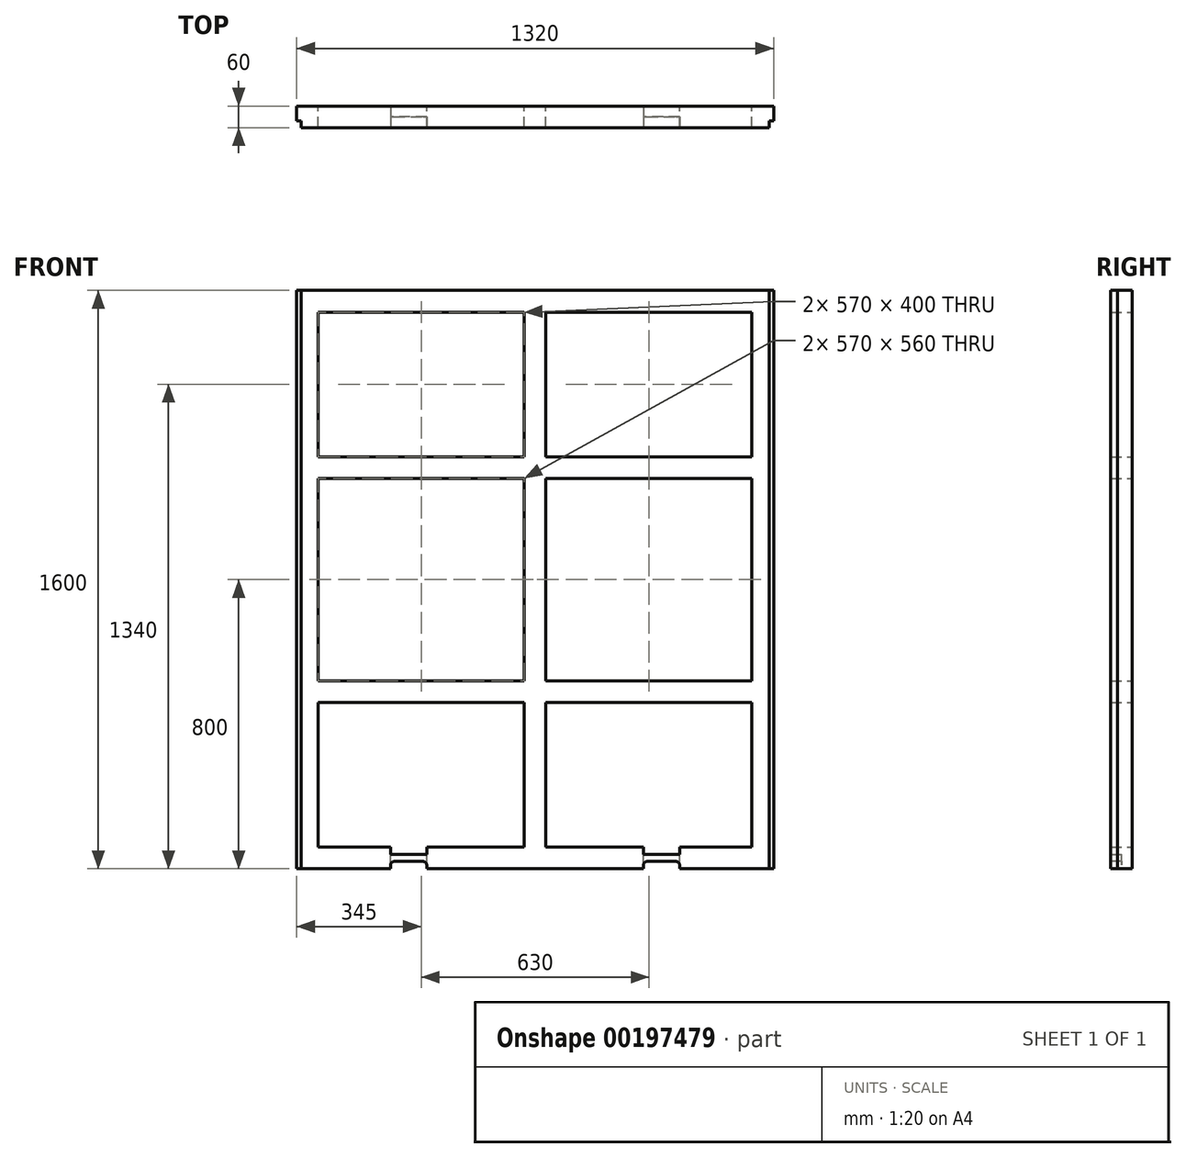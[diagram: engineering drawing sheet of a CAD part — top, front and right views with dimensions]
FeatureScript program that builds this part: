
annotation { "Feature Type Name" : "Feature", "Feature Type Description" : "" }
export const myFeature = defineFeature(function(context is Context, id is Id, definition is map)
    precondition{}
    {
        {
            var Q0;
            Q0=qCreatedBy(makeId("Front.planeOp"),FACE);
            var sketch = newSketch(context, id + "F0", { "sketchPlane" : qUnion([Q0])});
            skLineSegment(sketch, "E0.bottom", {"start": v(660, -800) * mm, "end": v(-660, -800) * mm});
            skLineSegment(sketch, "E0.top", {"start": v(660, 800) * mm, "end": v(-660, 800) * mm});
            skLineSegment(sketch, "E0.left", {"start": v(660, -800) * mm, "end": v(660, 800) * mm});
            skLineSegment(sketch, "E0.right", {"start": v(-660, -800) * mm, "end": v(-660, 800) * mm});
            skPoint(sketch, "E0.middle", {"position": v(0, 0) * mm});
            skLineSegment(sketch, "E1.0", {"start": v(600, 740) * mm, "end": v(30, 740) * mm});
            skLineSegment(sketch, "E1.1", {"start": v(600, -740) * mm, "end": v(600, -340) * mm});
            skLineSegment(sketch, "E1.2", {"start": v(600, -740) * mm, "end": v(30, -740) * mm});
            skLineSegment(sketch, "E1.3", {"start": v(-600, -740) * mm, "end": v(-600, -340) * mm});
            skLineSegment(sketch, "E2", {"start": v(-600, 340) * mm, "end": v(-30, 340) * mm});
            skLineSegment(sketch, "E3", {"start": v(-600, -340) * mm, "end": v(-30, -340) * mm});
            skLineSegment(sketch, "E4.0", {"start": v(-30, 740) * mm, "end": v(-30, 340) * mm});
            skLineSegment(sketch, "E5.0", {"start": v(30, 740) * mm, "end": v(30, 340) * mm});
            skLineSegment(sketch, "E6.0", {"start": v(-600, -280) * mm, "end": v(-30, -280) * mm});
            skPoint(sketch, "E7.orphan", {"position": v(0, 740) * mm});
            skLineSegment(sketch, "E8.trimOffspring", {"start": v(30, 340) * mm, "end": v(600, 340) * mm});
            skLineSegment(sketch, "E9.trimOffspring", {"start": v(-30, 280) * mm, "end": v(-30, -280) * mm});
            skLineSegment(sketch, "E10.trimOffspring", {"start": v(30, 280) * mm, "end": v(600, 280) * mm});
            skLineSegment(sketch, "E11.trimOffspring", {"start": v(30, 280) * mm, "end": v(30, -280) * mm});
            skLineSegment(sketch, "E12.trimOffspring", {"start": v(30, -280) * mm, "end": v(600, -280) * mm});
            skLineSegment(sketch, "E13.trimOffspring", {"start": v(30, -340) * mm, "end": v(30, -740) * mm});
            skLineSegment(sketch, "E14.trimOffspring", {"start": v(-30, -340) * mm, "end": v(-30, -740) * mm});
            skLineSegment(sketch, "E15.trimOffspring", {"start": v(30, -340) * mm, "end": v(600, -340) * mm});
            skPoint(sketch, "E16.orphan", {"position": v(0, -740) * mm});
            skLineSegment(sketch, "E17", {"start": v(-30, 280) * mm, "end": v(-600, 280) * mm});
            skLineSegment(sketch, "E18.trimOffspring", {"start": v(-30, 740) * mm, "end": v(-600, 740) * mm});
            skLineSegment(sketch, "E19.trimOffspring", {"start": v(600, 340) * mm, "end": v(600, 740) * mm});
            skLineSegment(sketch, "E20.trimOffspring", {"start": v(600, -280) * mm, "end": v(600, 280) * mm});
            skLineSegment(sketch, "E21.trimOffspring", {"start": v(-600, -280) * mm, "end": v(-600, 280) * mm});
            skLineSegment(sketch, "E22.trimOffspring", {"start": v(-600, 340) * mm, "end": v(-600, 740) * mm});
            skLineSegment(sketch, "E23.trimOffspring", {"start": v(-30, -740) * mm, "end": v(-600, -740) * mm});
            skSolve(sketch);
        }
        {
            var Q0;
            Q0 = qSketchRegion(id + "F0", true);
            extrude(context, id + "F1", {"entities" : qUnion([Q0]), "depth" : 60 * mm});
        }
        {
            var Q0;
            Q0=makeQuery(id+"F1.opExtrude","CAP_FACE",FACE,{"disambiguationData":[OSD([sQuery(id+"F0.wireOp",EDGE,"E0.bottom"),sQuery(id+"F0.wireOp",EDGE,"E0.top"),sQuery(id+"F0.wireOp",EDGE,"E0.left"),sQuery(id+"F0.wireOp",EDGE,"E0.right"),sQuery(id+"F0.wireOp",EDGE,"E1.0"),sQuery(id+"F0.wireOp",EDGE,"E1.1"),sQuery(id+"F0.wireOp",EDGE,"E1.2"),sQuery(id+"F0.wireOp",EDGE,"E1.3"),sQuery(id+"F0.wireOp",EDGE,"E2"),sQuery(id+"F0.wireOp",EDGE,"E3"),sQuery(id+"F0.wireOp",EDGE,"E4.0"),sQuery(id+"F0.wireOp",EDGE,"E5.0"),sQuery(id+"F0.wireOp",EDGE,"E6.0"),sQuery(id+"F0.wireOp",EDGE,"E8.trimOffspring"),sQuery(id+"F0.wireOp",EDGE,"E9.trimOffspring"),sQuery(id+"F0.wireOp",EDGE,"E10.trimOffspring"),sQuery(id+"F0.wireOp",EDGE,"E11.trimOffspring"),sQuery(id+"F0.wireOp",EDGE,"E12.trimOffspring"),sQuery(id+"F0.wireOp",EDGE,"E13.trimOffspring"),sQuery(id+"F0.wireOp",EDGE,"E14.trimOffspring"),sQuery(id+"F0.wireOp",EDGE,"E15.trimOffspring"),sQuery(id+"F0.wireOp",EDGE,"E17"),sQuery(id+"F0.wireOp",EDGE,"E18.trimOffspring"),sQuery(id+"F0.wireOp",EDGE,"E19.trimOffspring"),sQuery(id+"F0.wireOp",EDGE,"E20.trimOffspring"),sQuery(id+"F0.wireOp",EDGE,"E21.trimOffspring"),sQuery(id+"F0.wireOp",EDGE,"E22.trimOffspring"),sQuery(id+"F0.wireOp",EDGE,"E23.trimOffspring")])],"isStart":false});
            var sketch = newSketch(context, id + "F2", { "sketchPlane" : qUnion([Q0])});
            skLineSegment(sketch, "E24.bottom", {"start": v(-660, -800) * mm, "end": v(-648, -800) * mm});
            skLineSegment(sketch, "E24.top", {"start": v(-660, 800) * mm, "end": v(-648, 800) * mm});
            skLineSegment(sketch, "E24.left", {"start": v(-660, -800) * mm, "end": v(-660, 800) * mm});
            skLineSegment(sketch, "E24.right", {"start": v(-648, -800) * mm, "end": v(-648, 800) * mm});
            skLineSegment(sketch, "E25.bottom", {"start": v(660, -800) * mm, "end": v(648, -800) * mm});
            skLineSegment(sketch, "E25.top", {"start": v(660, 800) * mm, "end": v(648, 800) * mm});
            skLineSegment(sketch, "E25.left", {"start": v(660, -800) * mm, "end": v(660, 800) * mm});
            skLineSegment(sketch, "E25.right", {"start": v(648, -800) * mm, "end": v(648, 800) * mm});
            skSolve(sketch);
        }
        {
            var Q0;
            Q0 = qSketchRegion(id + "F2", true);
            extrude(context, id + "F3", {"entities" : qUnion([Q0]), "operationType" : NewBodyOperationType.REMOVE, "oppositeDirection" : true, "depth" : 19 * mm});
        }
        {
            var Q0;
            Q0=makeQuery(id+"F1.opExtrude","CAP_FACE",FACE,{"disambiguationData":[OSD([sQuery(id+"F0.wireOp",EDGE,"E0.bottom"),sQuery(id+"F0.wireOp",EDGE,"E0.top"),sQuery(id+"F0.wireOp",EDGE,"E0.left"),sQuery(id+"F0.wireOp",EDGE,"E0.right"),sQuery(id+"F0.wireOp",EDGE,"E1.0"),sQuery(id+"F0.wireOp",EDGE,"E1.1"),sQuery(id+"F0.wireOp",EDGE,"E1.2"),sQuery(id+"F0.wireOp",EDGE,"E1.3"),sQuery(id+"F0.wireOp",EDGE,"E2"),sQuery(id+"F0.wireOp",EDGE,"E3"),sQuery(id+"F0.wireOp",EDGE,"E4.0"),sQuery(id+"F0.wireOp",EDGE,"E5.0"),sQuery(id+"F0.wireOp",EDGE,"E6.0"),sQuery(id+"F0.wireOp",EDGE,"E8.trimOffspring"),sQuery(id+"F0.wireOp",EDGE,"E9.trimOffspring"),sQuery(id+"F0.wireOp",EDGE,"E10.trimOffspring"),sQuery(id+"F0.wireOp",EDGE,"E11.trimOffspring"),sQuery(id+"F0.wireOp",EDGE,"E12.trimOffspring"),sQuery(id+"F0.wireOp",EDGE,"E13.trimOffspring"),sQuery(id+"F0.wireOp",EDGE,"E14.trimOffspring"),sQuery(id+"F0.wireOp",EDGE,"E15.trimOffspring"),sQuery(id+"F0.wireOp",EDGE,"E17"),sQuery(id+"F0.wireOp",EDGE,"E18.trimOffspring"),sQuery(id+"F0.wireOp",EDGE,"E19.trimOffspring"),sQuery(id+"F0.wireOp",EDGE,"E20.trimOffspring"),sQuery(id+"F0.wireOp",EDGE,"E21.trimOffspring"),sQuery(id+"F0.wireOp",EDGE,"E22.trimOffspring"),sQuery(id+"F0.wireOp",EDGE,"E23.trimOffspring")])],"isStart":false});
            var sketch = newSketch(context, id + "F4", { "sketchPlane" : qUnion([Q0])});
            skLineSegment(sketch, "E26.bottom", {"start": v(-400, -800) * mm, "end": v(-300, -800) * mm});
            skLineSegment(sketch, "E26.top", {"start": v(-390, -780) * mm, "end": v(-310, -780) * mm});
            skLineSegment(sketch, "E26.left", {"start": v(-400, -800) * mm, "end": v(-400, -790) * mm});
            skLineSegment(sketch, "E26.right", {"start": v(-300, -800) * mm, "end": v(-300, -790) * mm});
            skLineSegment(sketch, "E27.bottom", {"start": v(300, -800) * mm, "end": v(400, -800) * mm});
            skLineSegment(sketch, "E27.top", {"start": v(310, -780) * mm, "end": v(390, -780) * mm});
            skLineSegment(sketch, "E27.left", {"start": v(300, -800) * mm, "end": v(300, -790) * mm});
            skLineSegment(sketch, "E27.right", {"start": v(400, -800) * mm, "end": v(400, -790) * mm});
            skPoint(sketch, "E28.visualSharp", {"position": v(-400, -780) * mm});
            skArc(sketch, "E28.filletArc", {"start": v(-390, -780) * mm, "mid": v(-397.07, -782.93) * mm, "end": v(-400, -790) * mm});
            skPoint(sketch, "E29.visualSharp", {"position": v(-300, -780) * mm});
            skArc(sketch, "E29.filletArc", {"start": v(-300, -790) * mm, "mid": v(-302.93, -782.93) * mm, "end": v(-310, -780) * mm});
            skPoint(sketch, "E30.visualSharp", {"position": v(300, -780) * mm});
            skArc(sketch, "E30.filletArc", {"start": v(310, -780) * mm, "mid": v(302.93, -782.93) * mm, "end": v(300, -790) * mm});
            skPoint(sketch, "E31.visualSharp", {"position": v(400, -780) * mm});
            skArc(sketch, "E31.filletArc", {"start": v(400, -790) * mm, "mid": v(397.07, -782.93) * mm, "end": v(390, -780) * mm});
            skSolve(sketch);
        }
        {
            var Q0;
            Q0 = qSketchRegion(id + "F4", true);
            extrude(context, id + "F5", {"entities" : qUnion([Q0]), "operationType" : NewBodyOperationType.REMOVE, "oppositeDirection" : true, "depth" : 60 * mm});
        }
        {
            var Q0;
            Q0=makeQuery(id+"F1.opExtrude","CAP_FACE",FACE,{"disambiguationData":[OSD([sQuery(id+"F0.wireOp",EDGE,"E0.bottom"),sQuery(id+"F0.wireOp",EDGE,"E0.top"),sQuery(id+"F0.wireOp",EDGE,"E0.left"),sQuery(id+"F0.wireOp",EDGE,"E0.right"),sQuery(id+"F0.wireOp",EDGE,"E1.0"),sQuery(id+"F0.wireOp",EDGE,"E1.1"),sQuery(id+"F0.wireOp",EDGE,"E1.2"),sQuery(id+"F0.wireOp",EDGE,"E1.3"),sQuery(id+"F0.wireOp",EDGE,"E2"),sQuery(id+"F0.wireOp",EDGE,"E3"),sQuery(id+"F0.wireOp",EDGE,"E4.0"),sQuery(id+"F0.wireOp",EDGE,"E5.0"),sQuery(id+"F0.wireOp",EDGE,"E6.0"),sQuery(id+"F0.wireOp",EDGE,"E8.trimOffspring"),sQuery(id+"F0.wireOp",EDGE,"E9.trimOffspring"),sQuery(id+"F0.wireOp",EDGE,"E10.trimOffspring"),sQuery(id+"F0.wireOp",EDGE,"E11.trimOffspring"),sQuery(id+"F0.wireOp",EDGE,"E12.trimOffspring"),sQuery(id+"F0.wireOp",EDGE,"E13.trimOffspring"),sQuery(id+"F0.wireOp",EDGE,"E14.trimOffspring"),sQuery(id+"F0.wireOp",EDGE,"E15.trimOffspring"),sQuery(id+"F0.wireOp",EDGE,"E17"),sQuery(id+"F0.wireOp",EDGE,"E18.trimOffspring"),sQuery(id+"F0.wireOp",EDGE,"E19.trimOffspring"),sQuery(id+"F0.wireOp",EDGE,"E20.trimOffspring"),sQuery(id+"F0.wireOp",EDGE,"E21.trimOffspring"),sQuery(id+"F0.wireOp",EDGE,"E22.trimOffspring"),sQuery(id+"F0.wireOp",EDGE,"E23.trimOffspring")])],"isStart":true});
            var sketch = newSketch(context, id + "F6", { "sketchPlane" : qUnion([Q0])});
            skLineSegment(sketch, "E32.bottom", {"start": v(-400, -800) * mm, "end": v(-300, -800) * mm});
            skLineSegment(sketch, "E32.top", {"start": v(-400, -740) * mm, "end": v(-300, -740) * mm});
            skLineSegment(sketch, "E32.left", {"start": v(-400, -800) * mm, "end": v(-400, -740) * mm});
            skLineSegment(sketch, "E32.right", {"start": v(-300, -800) * mm, "end": v(-300, -740) * mm});
            skLineSegment(sketch, "E33.bottom", {"start": v(300, -800) * mm, "end": v(400, -800) * mm});
            skLineSegment(sketch, "E33.top", {"start": v(300, -740) * mm, "end": v(400, -740) * mm});
            skLineSegment(sketch, "E33.left", {"start": v(300, -800) * mm, "end": v(300, -740) * mm});
            skLineSegment(sketch, "E33.right", {"start": v(400, -800) * mm, "end": v(400, -740) * mm});
            skSolve(sketch);
        }
        {
            var Q0;
            Q0 = qSketchRegion(id + "F6", true);
            extrude(context, id + "F7", {"entities" : qUnion([Q0]), "operationType" : NewBodyOperationType.REMOVE, "oppositeDirection" : true, "depth" : 30 * mm});
        }
        {
            var Q0;
            Q0=makeQuery(id+"F7.boolean.opBoolean","COPY",FACE,{"derivedFrom":makeQuery(id+"F7.opExtrude","CAP_FACE",FACE,{"disambiguationData":[OSD([sQuery(id+"F6.wireOp",EDGE,"E32.bottom"),sQuery(id+"F6.wireOp",EDGE,"E32.top"),sQuery(id+"F6.wireOp",EDGE,"E32.left"),sQuery(id+"F6.wireOp",EDGE,"E32.right")])],"isStart":false})});
            var sketch = newSketch(context, id + "F8", { "sketchPlane" : qUnion([Q0])});
            skLineSegment(sketch, "E34.bottom", {"start": v(-400, -740) * mm, "end": v(-300, -740) * mm});
            skLineSegment(sketch, "E34.top", {"start": v(-400, -760) * mm, "end": v(-300, -760) * mm});
            skLineSegment(sketch, "E34.left", {"start": v(-400, -740) * mm, "end": v(-400, -760) * mm});
            skLineSegment(sketch, "E34.right", {"start": v(-300, -740) * mm, "end": v(-300, -760) * mm});
            skSolve(sketch);
        }
        {
            var Q0;
            Q0 = qSketchRegion(id + "F8", true);
            extrude(context, id + "F9", {"entities" : qUnion([Q0]), "operationType" : NewBodyOperationType.REMOVE, "oppositeDirection" : true, "depth" : 30 * mm});
        }
        {
            var Q0;
            Q0=makeQuery(id+"F7.boolean.opBoolean","COPY",FACE,{"derivedFrom":makeQuery(id+"F7.opExtrude","CAP_FACE",FACE,{"disambiguationData":[OSD([sQuery(id+"F6.wireOp",EDGE,"E33.bottom"),sQuery(id+"F6.wireOp",EDGE,"E33.top"),sQuery(id+"F6.wireOp",EDGE,"E33.left"),sQuery(id+"F6.wireOp",EDGE,"E33.right")])],"isStart":false})});
            var sketch = newSketch(context, id + "F10", { "sketchPlane" : qUnion([Q0])});
            skLineSegment(sketch, "E35.bottom", {"start": v(300, -740) * mm, "end": v(400, -740) * mm});
            skLineSegment(sketch, "E35.top", {"start": v(300, -760) * mm, "end": v(400, -760) * mm});
            skLineSegment(sketch, "E35.left", {"start": v(300, -740) * mm, "end": v(300, -760) * mm});
            skLineSegment(sketch, "E35.right", {"start": v(400, -740) * mm, "end": v(400, -760) * mm});
            skSolve(sketch);
        }
        {
            var Q0;
            Q0 = qSketchRegion(id + "F10", true);
            extrude(context, id + "F11", {"entities" : qUnion([Q0]), "operationType" : NewBodyOperationType.REMOVE, "oppositeDirection" : true, "depth" : 30 * mm});
        }
    });
